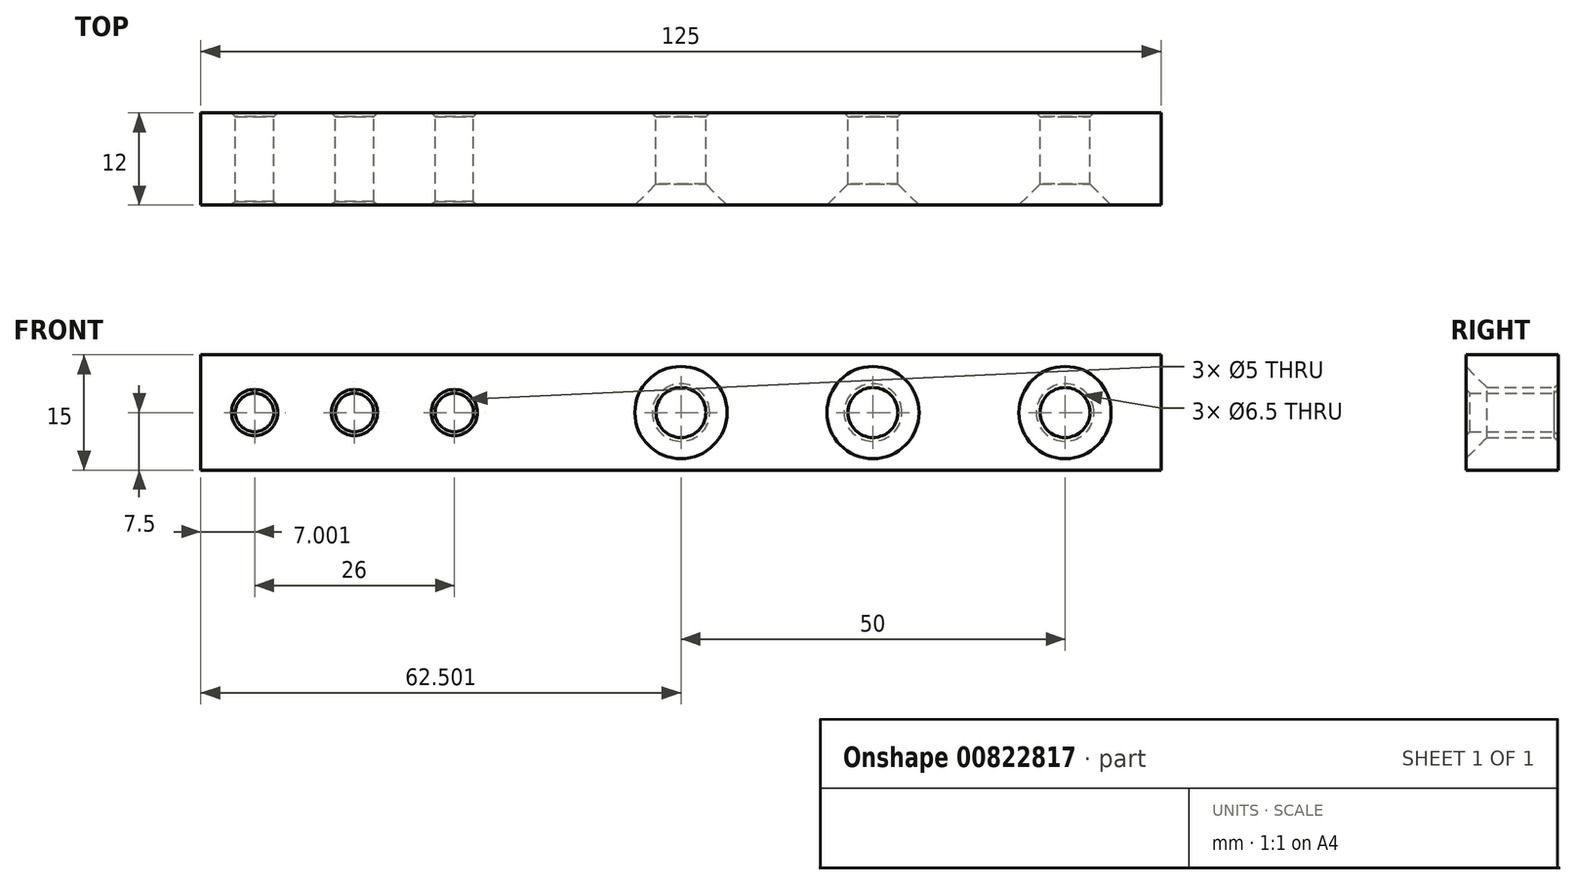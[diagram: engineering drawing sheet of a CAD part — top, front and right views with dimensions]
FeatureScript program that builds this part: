
annotation { "Feature Type Name" : "Feature", "Feature Type Description" : "" }
export const myFeature = defineFeature(function(context is Context, id is Id, definition is map)
    precondition{}
    {
        {
            var Q0;
            Q0=qCreatedBy(makeId("Front.planeOp"),FACE);
            var sketch = newSketch(context, id + "F0", { "sketchPlane" : qUnion([Q0])});
            skLineSegment(sketch, "E0", {"start": v(100.58, 0) * mm, "end": v(0, 0) * mm, "construction": true});
            skLineSegment(sketch, "E1", {"start": v(0, 0) * mm, "end": v(-43.94, 0) * mm, "construction": true});
            skLineSegment(sketch, "E2", {"start": v(-63.75, 0) * mm, "end": v(-63.75, 16.88) * mm, "construction": true});
            skLineSegment(sketch, "E3", {"start": v(3.75, 0) * mm, "end": v(3.75, 14.28) * mm, "construction": true});
            skCircle(sketch, "E4", {"center": v(-76.75, 0) * mm, "radius": 2.5 * mm});
            skCircle(sketch, "E5", {"center": v(-63.75, 0) * mm, "radius": 2.5 * mm});
            skCircle(sketch, "E6", {"center": v(3.75, 0) * mm, "radius": 3.25 * mm});
            skCircle(sketch, "E7", {"center": v(28.75, 0) * mm, "radius": 3.25 * mm});
            skCircle(sketch, "E8.MirrorC", {"center": v(-50.75, 0) * mm, "radius": 2.5 * mm});
            skCircle(sketch, "E9.MirrorC", {"center": v(-21.25, 0) * mm, "radius": 3.25 * mm});
            skLineSegment(sketch, "E10.bottom", {"start": v(-83.75, 7.5) * mm, "end": v(41.25, 7.5) * mm});
            skLineSegment(sketch, "E10.top", {"start": v(-83.75, -7.5) * mm, "end": v(41.25, -7.5) * mm});
            skLineSegment(sketch, "E10.left", {"start": v(-83.75, 7.5) * mm, "end": v(-83.75, -7.5) * mm});
            skLineSegment(sketch, "E10.right", {"start": v(41.25, 7.5) * mm, "end": v(41.25, -7.5) * mm});
            skSolve(sketch);
        }
        {
            var Q0;
            Q0 = qSketchRegion(id + "F0", true);
            extrude(context, id + "F1", {"entities" : qUnion([Q0]), "depth" : 12 * mm, "offsetDistance" : 25 * mm});
        }
        {
            var Q0;
            Q0=makeQuery(id+"F1.opExtrude","CAP_EDGE",EDGE,{"disambiguationData":[OSD([sQuery(id+"F0.wireOp",EDGE,"E9.MirrorC")])],"isStart":false});
            var Q1;
            Q1=makeQuery(id+"F1.opExtrude","CAP_EDGE",EDGE,{"disambiguationData":[OSD([sQuery(id+"F0.wireOp",EDGE,"E6")])],"isStart":false});
            var Q2;
            Q2=makeQuery(id+"F1.opExtrude","CAP_EDGE",EDGE,{"disambiguationData":[OSD([sQuery(id+"F0.wireOp",EDGE,"E7")])],"isStart":false});
            chamfer(context, id + "F2", {"entities" : qUnion([Q0, Q1, Q2]), "width" : 2.75 * mm, "tangentPropagation" : true});
        }
        {
            var Q0;
            Q0=makeQuery(id+"F1.opExtrude","CAP_EDGE",EDGE,{"disambiguationData":[OSD([sQuery(id+"F0.wireOp",EDGE,"E4")])],"isStart":false});
            var Q1;
            Q1=makeQuery(id+"F1.opExtrude","CAP_EDGE",EDGE,{"disambiguationData":[OSD([sQuery(id+"F0.wireOp",EDGE,"E5")])],"isStart":false});
            var Q2;
            Q2=makeQuery(id+"F1.opExtrude","CAP_EDGE",EDGE,{"disambiguationData":[OSD([sQuery(id+"F0.wireOp",EDGE,"E8.MirrorC")])],"isStart":false});
            var Q3;
            Q3=makeQuery(id+"F1.opExtrude","CAP_EDGE",EDGE,{"disambiguationData":[OSD([sQuery(id+"F0.wireOp",EDGE,"E6")])],"isStart":true});
            var Q4;
            Q4=makeQuery(id+"F1.opExtrude","CAP_EDGE",EDGE,{"disambiguationData":[OSD([sQuery(id+"F0.wireOp",EDGE,"E7")])],"isStart":true});
            var Q5;
            Q5=makeQuery(id+"F1.opExtrude","CAP_EDGE",EDGE,{"disambiguationData":[OSD([sQuery(id+"F0.wireOp",EDGE,"E9.MirrorC")])],"isStart":true});
            var Q6;
            Q6=makeQuery(id+"F1.opExtrude","CAP_EDGE",EDGE,{"disambiguationData":[OSD([sQuery(id+"F0.wireOp",EDGE,"E8.MirrorC")])],"isStart":true});
            var Q7;
            Q7=makeQuery(id+"F1.opExtrude","CAP_EDGE",EDGE,{"disambiguationData":[OSD([sQuery(id+"F0.wireOp",EDGE,"E5")])],"isStart":true});
            var Q8;
            Q8=makeQuery(id+"F1.opExtrude","CAP_EDGE",EDGE,{"disambiguationData":[OSD([sQuery(id+"F0.wireOp",EDGE,"E4")])],"isStart":true});
            chamfer(context, id + "F3", {"entities" : qUnion([Q0, Q1, Q2, Q3, Q4, Q5, Q6, Q7, Q8]), "width" : 0.5 * mm, "tangentPropagation" : true});
        }
    });
